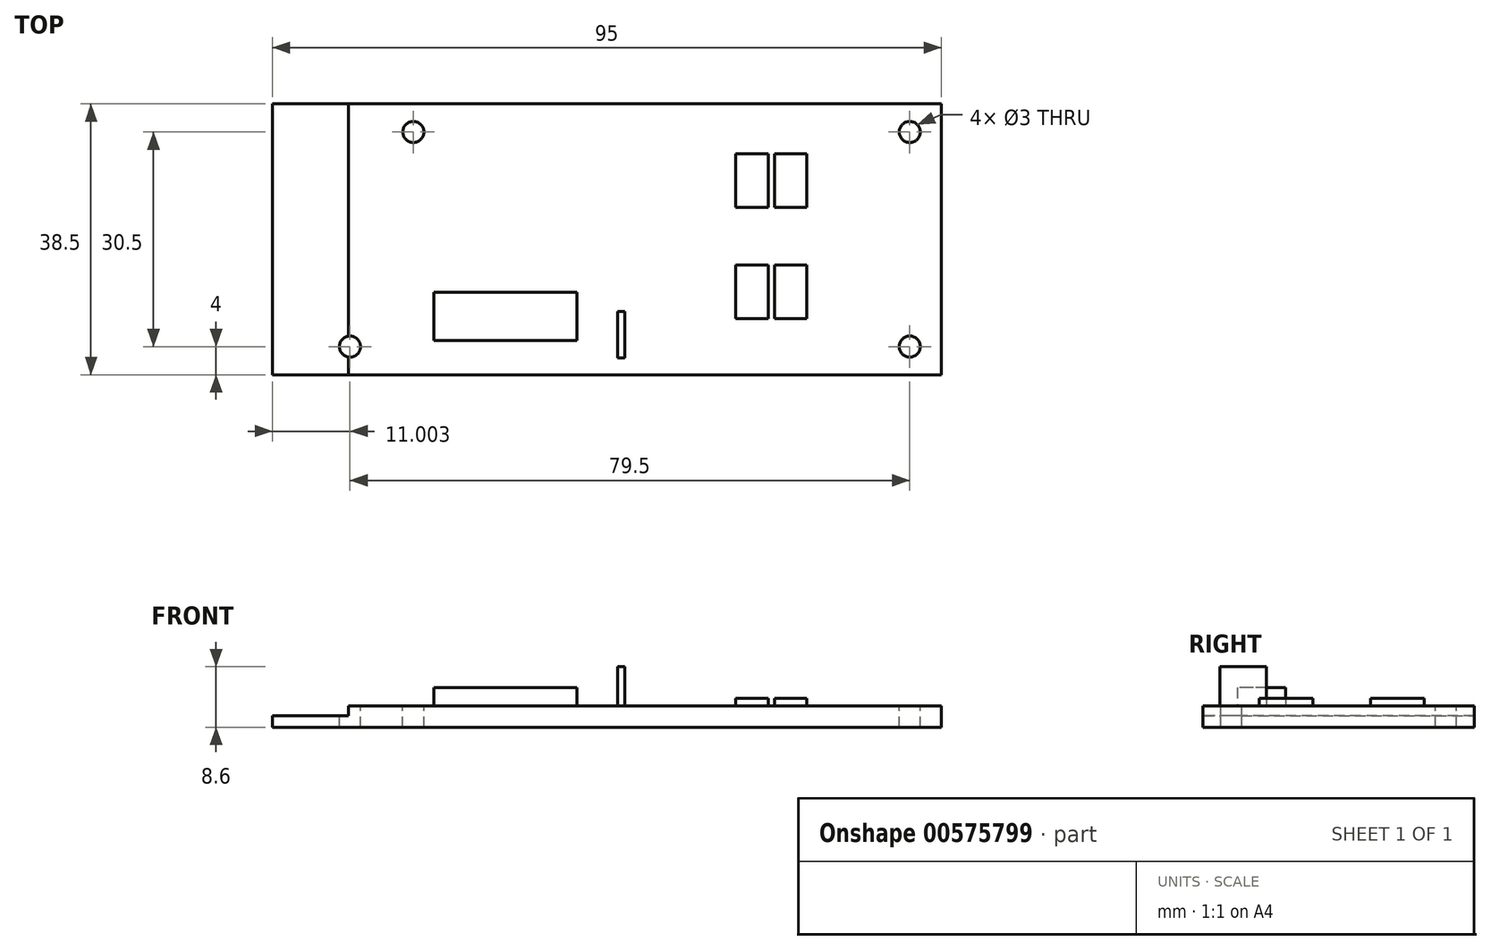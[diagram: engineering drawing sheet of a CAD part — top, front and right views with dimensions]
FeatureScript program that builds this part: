
annotation { "Feature Type Name" : "Feature", "Feature Type Description" : "" }
export const myFeature = defineFeature(function(context is Context, id is Id, definition is map)
    precondition{}
    {
        {
            var Q0;
            Q0=qCreatedBy(makeId("Top.planeOp"),FACE);
            var sketch = newSketch(context, id + "F0", { "sketchPlane" : qUnion([Q0])});
            skLineSegment(sketch, "E0.bottom", {"start": v(48.52, 19.25) * mm, "end": v(-46.48, 19.25) * mm});
            skLineSegment(sketch, "E0.top", {"start": v(48.52, -19.25) * mm, "end": v(-46.48, -19.25) * mm});
            skLineSegment(sketch, "E0.left", {"start": v(48.52, 19.25) * mm, "end": v(48.52, -19.25) * mm});
            skLineSegment(sketch, "E0.right", {"start": v(-46.48, 19.25) * mm, "end": v(-46.48, -19.25) * mm});
            skPoint(sketch, "E0.middle", {"position": v(1.02, 0) * mm});
            skSolve(sketch);
        }
        {
            var Q0;
            Q0=makeQuery(id+"F0.imprint","IMPRINT",FACE,{"disambiguationData":[TD([[makeQuery(id+"F0.imprint","IMPRINT",EDGE,{"derivedFrom":sQuery(id+"F0.wireOp",EDGE,"E0.bottom")}),1.0]])]});
            extrude(context, id + "F1", {"entities" : qUnion([Q0]), "depth" : 1.6 * mm, "offsetDistance" : 25.4 * mm});
        }
        {
            var Q0;
            Q0=makeQuery(id+"F1.opExtrude","CAP_FACE",FACE,{"disambiguationData":[OSD([sQuery(id+"F0.wireOp",EDGE,"E0.bottom"),sQuery(id+"F0.wireOp",EDGE,"E0.top"),sQuery(id+"F0.wireOp",EDGE,"E0.left"),sQuery(id+"F0.wireOp",EDGE,"E0.right")])],"isStart":false});
            var sketch = newSketch(context, id + "F2", { "sketchPlane" : qUnion([Q0])});
            skLineSegment(sketch, "E1.bottom", {"start": v(48.52, -19.25) * mm, "end": v(-35.68, -19.25) * mm});
            skLineSegment(sketch, "E1.top", {"start": v(48.52, 19.25) * mm, "end": v(-35.68, 19.25) * mm});
            skLineSegment(sketch, "E1.left", {"start": v(48.52, -19.25) * mm, "end": v(48.52, 19.25) * mm});
            skLineSegment(sketch, "E1.right", {"start": v(-35.68, -19.25) * mm, "end": v(-35.68, 19.25) * mm});
            skSolve(sketch);
        }
        {
            var Q0;
            Q0=makeQuery(id+"F2.imprint","IMPRINT",FACE,{"disambiguationData":[TD([[makeQuery(id+"F2.imprint","IMPRINT",EDGE,{"derivedFrom":sQuery(id+"F2.wireOp",EDGE,"E1.bottom")}),-1.0]])]});
            extrude(context, id + "F3", {"entities" : qUnion([Q0]), "operationType" : NewBodyOperationType.ADD, "depth" : 1.4 * mm, "offsetDistance" : 25.4 * mm});
        }
        {
            var Q0;
            Q0=makeQuery(id+"F3.opExtrude","CAP_FACE",FACE,{"disambiguationData":[OSD([sQuery(id+"F2.wireOp",EDGE,"E1.bottom"),sQuery(id+"F2.wireOp",EDGE,"E1.top"),sQuery(id+"F2.wireOp",EDGE,"E1.left"),sQuery(id+"F2.wireOp",EDGE,"E1.right")])],"isStart":false});
            var sketch = newSketch(context, id + "F4", { "sketchPlane" : qUnion([Q0])});
            skLineSegment(sketch, "E2.bottom", {"start": v(-3.22, -7.52) * mm, "end": v(-23.54, -7.52) * mm});
            skLineSegment(sketch, "E2.top", {"start": v(-3.22, -14.38) * mm, "end": v(-23.54, -14.38) * mm});
            skLineSegment(sketch, "E2.left", {"start": v(-3.22, -7.52) * mm, "end": v(-3.22, -14.38) * mm});
            skLineSegment(sketch, "E2.right", {"start": v(-23.54, -7.52) * mm, "end": v(-23.54, -14.38) * mm});
            skPoint(sketch, "E2.middle", {"position": v(-13.38, -10.95) * mm});
            skSolve(sketch);
        }
        {
            var Q0;
            Q0=makeQuery(id+"F4.imprint","IMPRINT",FACE,{"disambiguationData":[TD([[makeQuery(id+"F4.imprint","IMPRINT",EDGE,{"derivedFrom":sQuery(id+"F4.wireOp",EDGE,"E2.bottom")}),1.0]])]});
            extrude(context, id + "F5", {"entities" : qUnion([Q0]), "operationType" : NewBodyOperationType.ADD, "depth" : 2.6 * mm, "offsetDistance" : 25.4 * mm});
        }
        {
            var Q0;
            Q0=makeQuery(id+"F3.opExtrude","CAP_FACE",FACE,{"disambiguationData":[OSD([sQuery(id+"F2.wireOp",EDGE,"E1.bottom"),sQuery(id+"F2.wireOp",EDGE,"E1.top"),sQuery(id+"F2.wireOp",EDGE,"E1.left"),sQuery(id+"F2.wireOp",EDGE,"E1.right")])],"isStart":false});
            var sketch = newSketch(context, id + "F6", { "sketchPlane" : qUnion([Q0])});
            skLineSegment(sketch, "E3.bottom", {"start": v(23.92, 12.15) * mm, "end": v(19.32, 12.15) * mm});
            skLineSegment(sketch, "E3.top", {"start": v(23.92, 4.55) * mm, "end": v(19.32, 4.55) * mm});
            skLineSegment(sketch, "E3.left", {"start": v(23.92, 12.15) * mm, "end": v(23.92, 4.55) * mm});
            skLineSegment(sketch, "E3.right", {"start": v(19.32, 12.15) * mm, "end": v(19.32, 4.55) * mm});
            skPoint(sketch, "E3.middle", {"position": v(21.62, 8.35) * mm});
            skLineSegment(sketch, "E4.bottom", {"start": v(29.42, 12.15) * mm, "end": v(24.82, 12.15) * mm});
            skLineSegment(sketch, "E4.top", {"start": v(29.42, 4.55) * mm, "end": v(24.82, 4.55) * mm});
            skLineSegment(sketch, "E4.left", {"start": v(29.42, 12.15) * mm, "end": v(29.42, 4.55) * mm});
            skLineSegment(sketch, "E4.right", {"start": v(24.82, 12.15) * mm, "end": v(24.82, 4.55) * mm});
            skPoint(sketch, "E4.middle", {"position": v(27.12, 8.35) * mm});
            skLineSegment(sketch, "E5.bottom", {"start": v(23.92, -11.25) * mm, "end": v(19.32, -11.25) * mm});
            skLineSegment(sketch, "E5.top", {"start": v(23.92, -3.65) * mm, "end": v(19.32, -3.65) * mm});
            skLineSegment(sketch, "E5.left", {"start": v(23.92, -11.25) * mm, "end": v(23.92, -3.65) * mm});
            skLineSegment(sketch, "E5.right", {"start": v(19.32, -11.25) * mm, "end": v(19.32, -3.65) * mm});
            skPoint(sketch, "E5.middle", {"position": v(21.62, -7.45) * mm});
            skLineSegment(sketch, "E6.bottom", {"start": v(29.42, -11.25) * mm, "end": v(24.82, -11.25) * mm});
            skLineSegment(sketch, "E6.top", {"start": v(29.42, -3.65) * mm, "end": v(24.82, -3.65) * mm});
            skLineSegment(sketch, "E6.left", {"start": v(29.42, -11.25) * mm, "end": v(29.42, -3.65) * mm});
            skLineSegment(sketch, "E6.right", {"start": v(24.82, -11.25) * mm, "end": v(24.82, -3.65) * mm});
            skPoint(sketch, "E6.middle", {"position": v(27.12, -7.45) * mm});
            skLineSegment(sketch, "E7", {"start": v(14.02, 8.35) * mm, "end": v(35.82, 8.35) * mm, "construction": true});
            skLineSegment(sketch, "E8", {"start": v(21.62, 13.96) * mm, "end": v(21.62, -24.53) * mm, "construction": true});
            skLineSegment(sketch, "E9", {"start": v(16.18, -7.45) * mm, "end": v(38.56, -7.45) * mm, "construction": true});
            skLineSegment(sketch, "E10", {"start": v(27.12, 13.93) * mm, "end": v(27.12, -20.73) * mm, "construction": true});
            skSolve(sketch);
        }
        {
            var Q0;
            Q0=makeQuery(id+"F6.imprint","IMPRINT",FACE,{"disambiguationData":[TD([[makeQuery(id+"F6.imprint","IMPRINT",EDGE,{"derivedFrom":sQuery(id+"F6.wireOp",EDGE,"E6.bottom")}),-1.0]])]});
            var Q1;
            Q1=makeQuery(id+"F6.imprint","IMPRINT",FACE,{"disambiguationData":[TD([[makeQuery(id+"F6.imprint","IMPRINT",EDGE,{"derivedFrom":sQuery(id+"F6.wireOp",EDGE,"E5.bottom")}),-1.0]])]});
            var Q2;
            Q2=makeQuery(id+"F6.imprint","IMPRINT",FACE,{"disambiguationData":[TD([[makeQuery(id+"F6.imprint","IMPRINT",EDGE,{"derivedFrom":sQuery(id+"F6.wireOp",EDGE,"E3.bottom")}),1.0]])]});
            var Q3;
            Q3=makeQuery(id+"F6.imprint","IMPRINT",FACE,{"disambiguationData":[TD([[makeQuery(id+"F6.imprint","IMPRINT",EDGE,{"derivedFrom":sQuery(id+"F6.wireOp",EDGE,"E4.bottom")}),1.0]])]});
            extrude(context, id + "F7", {"entities" : qUnion([Q0, Q1, Q2, Q3]), "operationType" : NewBodyOperationType.ADD, "depth" : 1.1 * mm, "offsetDistance" : 25.4 * mm});
        }
        {
            var Q0;
            Q0=makeQuery(id+"F3.opExtrude","CAP_FACE",FACE,{"disambiguationData":[OSD([sQuery(id+"F2.wireOp",EDGE,"E1.bottom"),sQuery(id+"F2.wireOp",EDGE,"E1.top"),sQuery(id+"F2.wireOp",EDGE,"E1.left"),sQuery(id+"F2.wireOp",EDGE,"E1.right")])],"isStart":false});
            var sketch = newSketch(context, id + "F8", { "sketchPlane" : qUnion([Q0])});
            skLineSegment(sketch, "E11.bottom", {"start": v(3.54, -10.25) * mm, "end": v(2.54, -10.25) * mm});
            skLineSegment(sketch, "E11.top", {"start": v(3.54, -16.85) * mm, "end": v(2.54, -16.85) * mm});
            skLineSegment(sketch, "E11.left", {"start": v(3.54, -10.25) * mm, "end": v(3.54, -16.85) * mm});
            skLineSegment(sketch, "E11.right", {"start": v(2.54, -10.25) * mm, "end": v(2.54, -16.85) * mm});
            skPoint(sketch, "E11.middle", {"position": v(3.04, -13.55) * mm});
            skSolve(sketch);
        }
        {
            var Q0;
            Q0=makeQuery(id+"F8.imprint","IMPRINT",FACE,{"disambiguationData":[TD([[makeQuery(id+"F8.imprint","IMPRINT",EDGE,{"derivedFrom":sQuery(id+"F8.wireOp",EDGE,"E11.bottom")}),1.0]])]});
            extrude(context, id + "F9", {"entities" : qUnion([Q0]), "operationType" : NewBodyOperationType.ADD, "depth" : 5.6 * mm, "offsetDistance" : 25.4 * mm});
        }
        {
            var Q0;
            Q0=makeQuery(id+"F3.opExtrude","CAP_FACE",FACE,{"disambiguationData":[OSD([sQuery(id+"F2.wireOp",EDGE,"E1.bottom"),sQuery(id+"F2.wireOp",EDGE,"E1.top"),sQuery(id+"F2.wireOp",EDGE,"E1.left"),sQuery(id+"F2.wireOp",EDGE,"E1.right")])],"isStart":false});
            var sketch = newSketch(context, id + "F10", { "sketchPlane" : qUnion([Q0])});
            skCircle(sketch, "E12", {"center": v(-26.48, 15.25) * mm, "radius": 1.5 * mm});
            skCircle(sketch, "E13", {"center": v(-35.48, -15.25) * mm, "radius": 1.5 * mm});
            skCircle(sketch, "E14", {"center": v(44.02, 15.25) * mm, "radius": 1.5 * mm});
            skCircle(sketch, "E15", {"center": v(44.02, -15.25) * mm, "radius": 1.5 * mm});
            skSolve(sketch);
        }
        {
            var Q0;
            Q0=makeQuery(id+"F10.imprint","IMPRINT",FACE,{"disambiguationData":[TD([[makeQuery(id+"F10.imprint","IMPRINT",EDGE,{"derivedFrom":sQuery(id+"F10.wireOp",EDGE,"E12")}),1.0]])]});
            var Q1;
            {var subQ0=sQuery(id+"F10.wireOp",EDGE,"E13");var subQ1=makeQuery(id+"F3.opExtrude","CAP_EDGE",EDGE,{"disambiguationData":[OSD([sQuery(id+"F2.wireOp",EDGE,"E1.right")])],"isStart":false});var subQ2=makeQuery(id+"F10.imprint","INTERSECT",VERTEX,{"disambiguationData":[OD(0.0)],"derivedFrom":[subQ1,subQ0]});Q1=makeQuery(id+"F10.imprint","IMPRINT",FACE,{"disambiguationData":[TD([[makeQuery(id+"F10.imprint","IMPRINT",EDGE,{"disambiguationData":[TD([[subQ2,1.0]])],"derivedFrom":subQ0}),1.0]])]});}
            var Q2;
            {var subQ0=sQuery(id+"F10.wireOp",EDGE,"E13");var subQ1=makeQuery(id+"F3.opExtrude","CAP_EDGE",EDGE,{"disambiguationData":[OSD([sQuery(id+"F2.wireOp",EDGE,"E1.right")])],"isStart":false});var subQ2=makeQuery(id+"F10.imprint","INTERSECT",VERTEX,{"disambiguationData":[OD(0.0)],"derivedFrom":[subQ1,subQ0]});Q2=makeQuery(id+"F10.imprint","IMPRINT",FACE,{"disambiguationData":[TD([[makeQuery(id+"F10.imprint","IMPRINT",EDGE,{"disambiguationData":[TD([[subQ2,-1.0]])],"derivedFrom":subQ0}),1.0]])]});}
            var Q3;
            Q3=makeQuery(id+"F10.imprint","IMPRINT",FACE,{"disambiguationData":[TD([[makeQuery(id+"F10.imprint","IMPRINT",EDGE,{"derivedFrom":sQuery(id+"F10.wireOp",EDGE,"E14")}),1.0]])]});
            var Q4;
            Q4=makeQuery(id+"F10.imprint","IMPRINT",FACE,{"disambiguationData":[TD([[makeQuery(id+"F10.imprint","IMPRINT",EDGE,{"derivedFrom":sQuery(id+"F10.wireOp",EDGE,"E15")}),1.0]])]});
            extrude(context, id + "F11", {"entities" : qUnion([Q0, Q1, Q2, Q3, Q4]), "operationType" : NewBodyOperationType.REMOVE, "oppositeDirection" : true, "depth" : 3 * mm, "offsetDistance" : 25.4 * mm});
        }
    });
